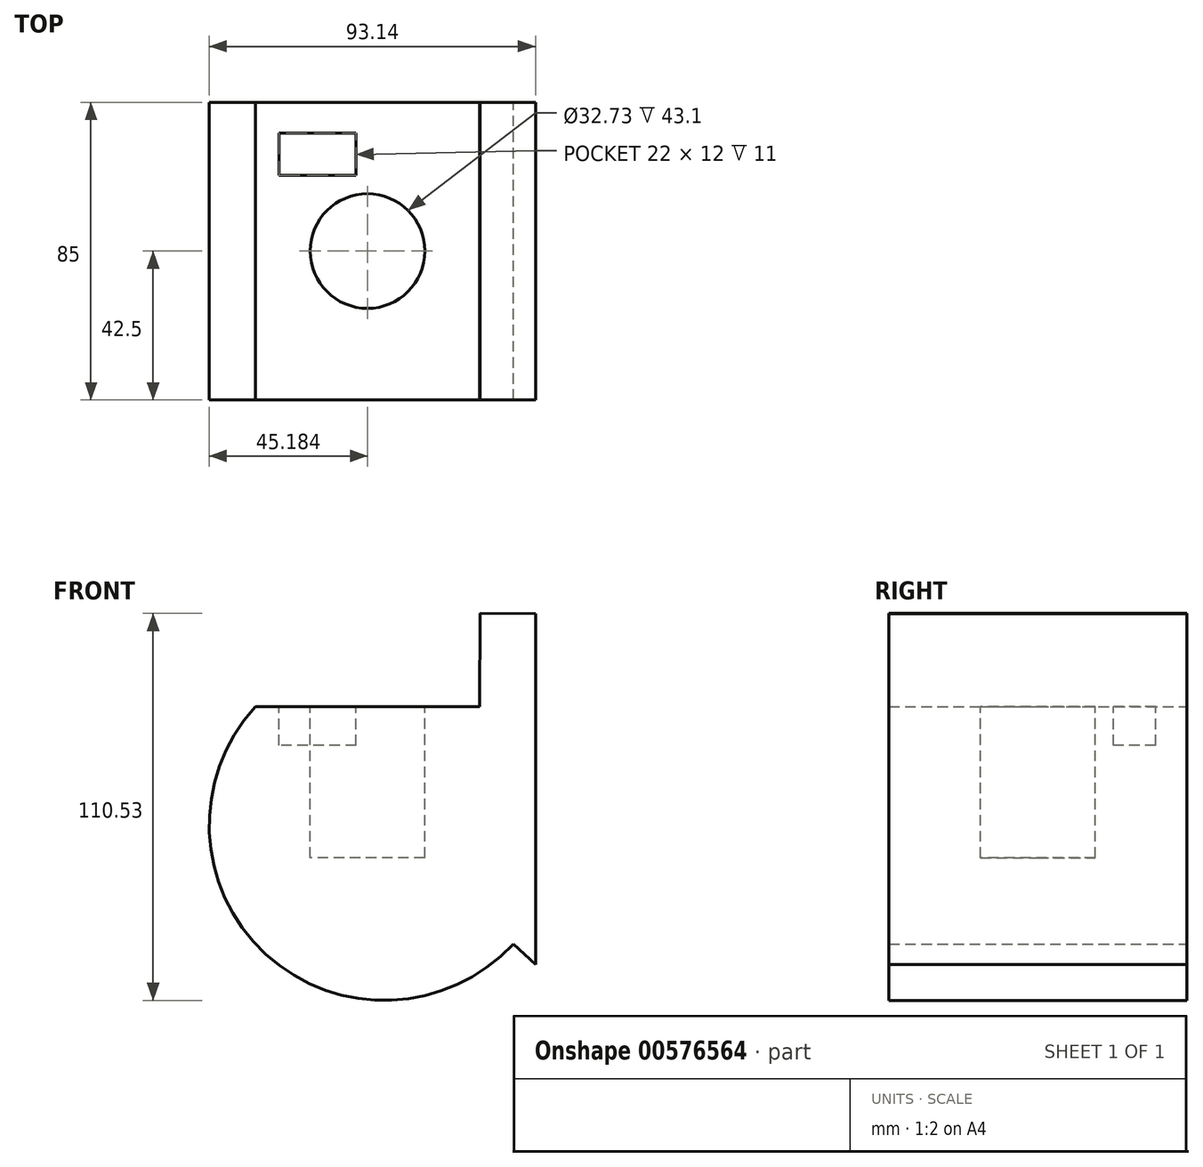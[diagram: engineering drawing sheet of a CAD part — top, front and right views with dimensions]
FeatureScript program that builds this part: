
annotation { "Feature Type Name" : "Feature", "Feature Type Description" : "" }
export const myFeature = defineFeature(function(context is Context, id is Id, definition is map)
    precondition{}
    {
        {
            var Q0;
            Q0=qCreatedBy(makeId("Front.planeOp"),FACE);
            var sketch = newSketch(context, id + "F0", { "sketchPlane" : qUnion([Q0])});
            skLineSegment(sketch, "E0", {"start": v(17.62, -9.5) * mm, "end": v(23.97, -15.35) * mm});
            skLineSegment(sketch, "E1", {"start": v(-55.95, 58.22) * mm, "end": v(7.98, 58.22) * mm});
            skLineSegment(sketch, "E2", {"start": v(8.2, 84.89) * mm, "end": v(7.98, 58.22) * mm});
            skLineSegment(sketch, "E3", {"start": v(8.2, 84.89) * mm, "end": v(23.97, 84.76) * mm});
            skLineSegment(sketch, "E4", {"start": v(23.97, 84.76) * mm, "end": v(23.97, -15.35) * mm});
            skArc(sketch, "E5", {"start": v(-55.95, 58.22) * mm, "mid": v(-53.03, -12.43) * mm, "end": v(17.62, -9.5) * mm});
            skSolve(sketch);
        }
        {
            var Q0;
            Q0 = qSketchRegion(id + "F0", true);
            extrude(context, id + "F1", {"entities" : qUnion([Q0]), "depth" : 85 * mm, "offsetDistance" : 25 * mm});
        }
        {
            var Q0;
            Q0=makeQuery(id+"F1.opExtrude","SWEPT_FACE",FACE,{"disambiguationData":[OSD([sQuery(id+"F0.wireOp",EDGE,"E1")])]});
            var sketch = newSketch(context, id + "F2", { "sketchPlane" : qUnion([Q0])});
            skCircle(sketch, "E6", {"center": v(-23.99, -42.5) * mm, "radius": 16.37 * mm});
            skLineSegment(sketch, "E7", {"start": v(-55.95, -42.5) * mm, "end": v(7.98, -42.5) * mm, "construction": true});
            skLineSegment(sketch, "E8", {"start": v(-23.99, -85) * mm, "end": v(-23.99, 0) * mm, "construction": true});
            skSolve(sketch);
        }
        {
            var Q0;
            Q0=makeQuery(id+"F2.imprint","IMPRINT",FACE,{"disambiguationData":[TD([[makeQuery(id+"F2.imprint","IMPRINT",EDGE,{"derivedFrom":sQuery(id+"F2.wireOp",EDGE,"E6")}),1.0]])]});
            extrude(context, id + "F3", {"entities" : qUnion([Q0]), "operationType" : NewBodyOperationType.REMOVE, "oppositeDirection" : true, "depth" : 43.1 * mm, "offsetDistance" : 25 * mm});
        }
        {
            var Q0;
            Q0=makeQuery(id+"F1.opExtrude","SWEPT_FACE",FACE,{"disambiguationData":[OSD([sQuery(id+"F0.wireOp",EDGE,"E1")])]});
            var sketch = newSketch(context, id + "F4", { "sketchPlane" : qUnion([Q0])});
            skLineSegment(sketch, "E9.bottom", {"start": v(-27.23, -8.86) * mm, "end": v(-49.23, -8.86) * mm});
            skLineSegment(sketch, "E9.top", {"start": v(-27.23, -20.86) * mm, "end": v(-49.23, -20.86) * mm});
            skLineSegment(sketch, "E9.left", {"start": v(-27.23, -8.86) * mm, "end": v(-27.23, -20.86) * mm});
            skLineSegment(sketch, "E9.right", {"start": v(-49.23, -8.86) * mm, "end": v(-49.23, -20.86) * mm});
            skPoint(sketch, "E9.middle", {"position": v(-38.23, -14.86) * mm});
            skSolve(sketch);
        }
        {
            var Q0;
            Q0=makeQuery(id+"F4.imprint","IMPRINT",FACE,{"disambiguationData":[TD([[makeQuery(id+"F4.imprint","IMPRINT",EDGE,{"derivedFrom":sQuery(id+"F4.wireOp",EDGE,"E9.bottom")}),1.0]])]});
            extrude(context, id + "F5", {"entities" : qUnion([Q0]), "operationType" : NewBodyOperationType.REMOVE, "oppositeDirection" : true, "depth" : 11 * mm, "offsetDistance" : 25 * mm});
        }
    });
